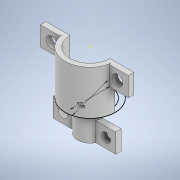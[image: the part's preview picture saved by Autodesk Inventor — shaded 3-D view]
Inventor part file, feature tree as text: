
AUTODESK INVENTOR PART (.ipt)
format: ipt  version: 2020.2 (Build 242310000, 310)  size: 292,352 bytes
history: native  units: in
note: dims shown in document units (in); Inventor stores cm internally (conversion verified against a paired STEP export)
features: sketch x12, extrude x9, hole x2, projected_geometry x2
ambient origin geometry x8: Origin, YZ Plane, XZ Plane, XY Plane, X Axis, Y Axis, Z Axis, Center Point
bodies: Body1 (feature_tree)
feature tree (25):
  extrude  "Extrusion2"  Depth=0.3543in
  extrude  "Extrusion3"  Depth=0.0394in
  extrude  "Extrusion4"  Depth=0.0394in TaperAngle=0.0deg
  sketch  "Sketch11"  dims[d20=0.0394in d59=0.5709in]
  sketch  "Sketch12"  dims[d60=0.7087in d61=0.0787in d62=0.0in]
  extrude  "Extrusion11"  Depth=0.0394in
  extrude  "Extrusion12"  Depth=0.0787in TaperAngle=0.0deg
  sketch  "Sketch14"  dims[d63=0.6299in d64=0.0in d72=0.0039in]
  extrude  "Extrusion14"  Depth=0.6299in
  hole  "Hole1"  [1 undecoded]
  extrude  "Extrusion16"  Depth=0.1575in
  hole  "Hole2"  [1 undecoded]
  extrude  "Extrusion17"  Depth=0.2756in TaperAngle=0.0deg
  extrude  "Extrusion18"  Depth=0.0787in
  sketch  "Sketch3"  dims[d10=0.3543in d11=0.2047in]
  sketch  "Sketch4"  dims[d12=0.1575in d13=0.0in d14=0.0394in]
  projected_geometry  "Projected Loop1"
  sketch  "Sketch5"  dims[d16=0.2362in d17=0.0in d18=0.0394in d19=0.0in]
  sketch  "Sketch15"  dims[d73=0.2756in d74=0.2756in]
  sketch  "Sketch17"  dims[d75=0.2756in d76=0.0in d81=0.1575in]
  sketch  "Sketch18"  dims[d82=0.1575in]
  sketch  "Sketch19"  dims[d83=0.1535in d84=0.75in d85=0.323in d86=0.25in d87=90.0deg d88=1.0in d89=0.8108in d90=0.2756in]
  sketch  "Sketch20"  dims[d91=0.2756in d92=0.2756in d93=0.0in]
  sketch  "Sketch21"  dims[d94=0.1378in d95=0.1378in d96=0.1339in d97=0.75in d98=0.248in d99=0.25in d100=90.0deg d101=1.0in d102=0.8108in d103=5.0in d104=0.0in d105=0.0787in d106=0.0in d107=0.5in d108=0.0344in d109=0.5in d110=0.0344in]
  projected_geometry  "Projected Loop3"
note: 2 required parameter values undecoded (feature->parameter linkage not recoverable at this tier; creation-order binding heuristic only, values carry confidence <= 0.55)
